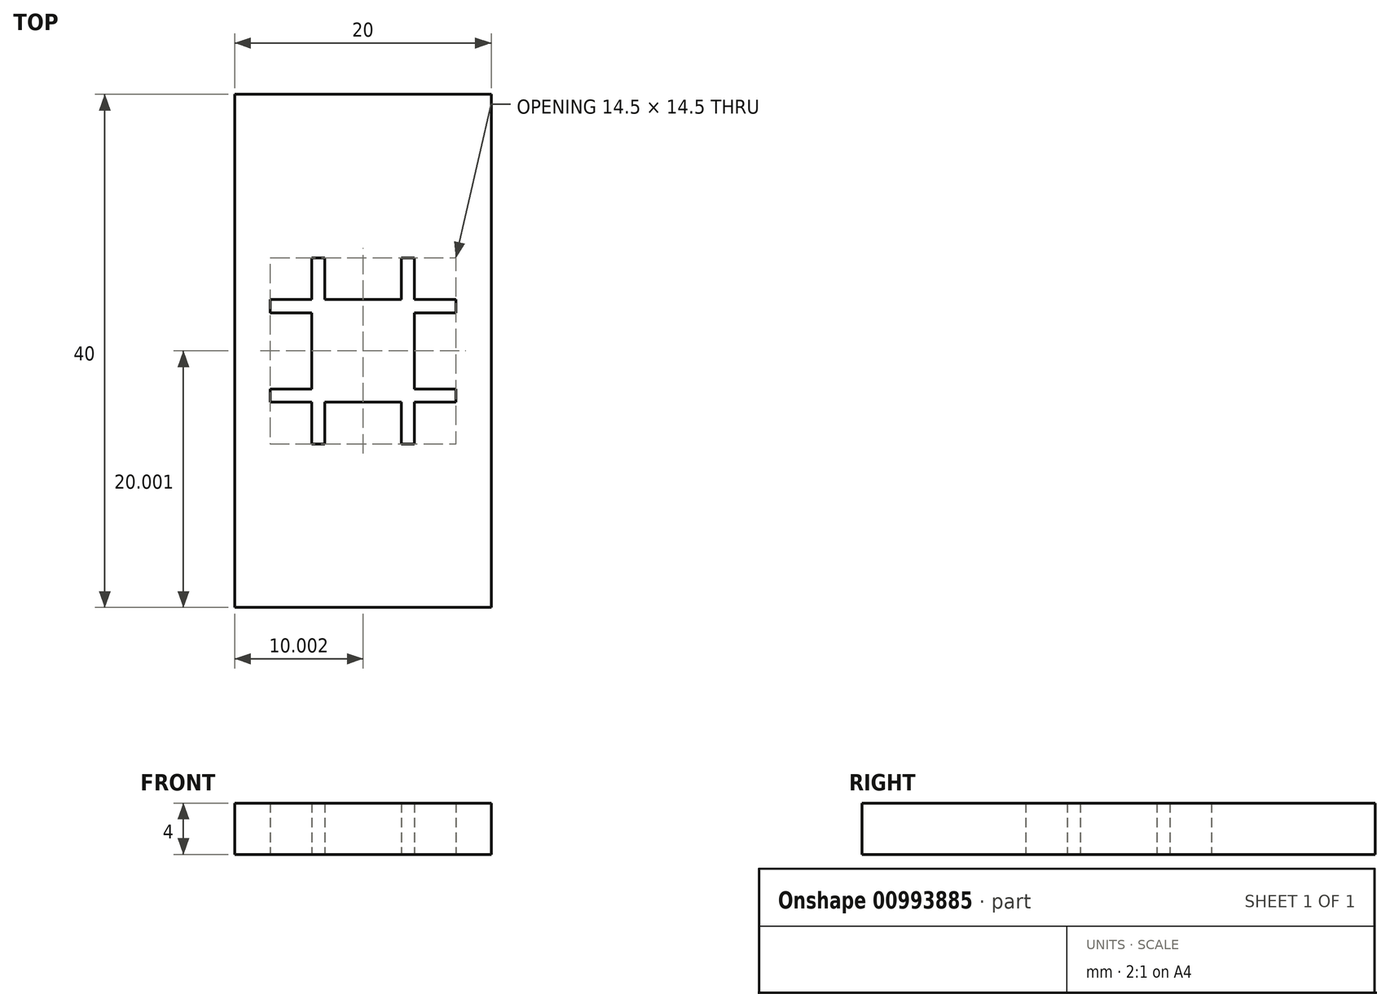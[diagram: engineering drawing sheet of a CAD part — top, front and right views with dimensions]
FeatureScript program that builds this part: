
annotation { "Feature Type Name" : "Feature", "Feature Type Description" : "" }
export const myFeature = defineFeature(function(context is Context, id is Id, definition is map)
    precondition{}
    {
        {
            var Q0;
            Q0=qCreatedBy(makeId("Top.planeOp"),FACE);
            var sketch = newSketch(context, id + "F0", { "sketchPlane" : qUnion([Q0])});
            skLineSegment(sketch, "E0", {"start": v(-4.23, 9.21) * mm, "end": v(-4.23, 12.46) * mm});
            skLineSegment(sketch, "E1", {"start": v(-4.23, 12.46) * mm, "end": v(-5.25, 12.46) * mm});
            skLineSegment(sketch, "E2", {"start": v(-5.25, 12.46) * mm, "end": v(-5.25, 9.21) * mm});
            skLineSegment(sketch, "E3", {"start": v(-5.25, 9.21) * mm, "end": v(-8.5, 9.21) * mm});
            skLineSegment(sketch, "E4", {"start": v(-8.5, 9.21) * mm, "end": v(-8.5, 8.2) * mm});
            skLineSegment(sketch, "E5", {"start": v(-8.5, 8.2) * mm, "end": v(-5.25, 8.2) * mm});
            skLineSegment(sketch, "E6", {"start": v(-5.25, 8.2) * mm, "end": v(-5.25, 2.23) * mm});
            skLineSegment(sketch, "E7", {"start": v(-5.25, 2.23) * mm, "end": v(-8.5, 2.23) * mm});
            skLineSegment(sketch, "E8", {"start": v(-8.5, 2.23) * mm, "end": v(-8.5, 1.21) * mm});
            skLineSegment(sketch, "E9", {"start": v(-8.5, 1.21) * mm, "end": v(-5.25, 1.21) * mm});
            skLineSegment(sketch, "E10", {"start": v(-5.25, 1.21) * mm, "end": v(-5.25, -2.04) * mm});
            skLineSegment(sketch, "E11", {"start": v(-5.25, -2.04) * mm, "end": v(-4.23, -2.04) * mm});
            skLineSegment(sketch, "E12", {"start": v(-4.23, -2.04) * mm, "end": v(-4.23, 1.21) * mm});
            skLineSegment(sketch, "E13", {"start": v(-4.23, 1.21) * mm, "end": v(1.73, 1.21) * mm});
            skLineSegment(sketch, "E14", {"start": v(1.73, 1.21) * mm, "end": v(1.73, -2.04) * mm});
            skLineSegment(sketch, "E15", {"start": v(1.73, -2.04) * mm, "end": v(2.75, -2.04) * mm});
            skLineSegment(sketch, "E16", {"start": v(2.75, -2.04) * mm, "end": v(2.75, 1.21) * mm});
            skLineSegment(sketch, "E17", {"start": v(2.75, 1.21) * mm, "end": v(6, 1.21) * mm});
            skLineSegment(sketch, "E18", {"start": v(6, 1.21) * mm, "end": v(6, 2.23) * mm});
            skLineSegment(sketch, "E19", {"start": v(6, 2.23) * mm, "end": v(2.75, 2.23) * mm});
            skLineSegment(sketch, "E20", {"start": v(2.75, 2.23) * mm, "end": v(2.75, 8.2) * mm});
            skLineSegment(sketch, "E21", {"start": v(2.75, 8.2) * mm, "end": v(6, 8.2) * mm});
            skLineSegment(sketch, "E22", {"start": v(6, 8.2) * mm, "end": v(6, 9.21) * mm});
            skLineSegment(sketch, "E23", {"start": v(6, 9.21) * mm, "end": v(2.75, 9.21) * mm});
            skLineSegment(sketch, "E24", {"start": v(2.75, 9.21) * mm, "end": v(2.75, 12.46) * mm});
            skLineSegment(sketch, "E25", {"start": v(2.75, 12.46) * mm, "end": v(1.73, 12.46) * mm});
            skLineSegment(sketch, "E26", {"start": v(1.73, 12.46) * mm, "end": v(1.73, 9.21) * mm});
            skLineSegment(sketch, "E27", {"start": v(1.73, 9.21) * mm, "end": v(-4.23, 9.21) * mm});
            skLineSegment(sketch, "E28", {"start": v(-1.25, 9.21) * mm, "end": v(-1.25, 1.21) * mm, "construction": true});
            skLineSegment(sketch, "E29", {"start": v(-5.25, 5.21) * mm, "end": v(2.75, 5.21) * mm, "construction": true});
            skLineSegment(sketch, "E30.bottom", {"start": v(8.75, -14.79) * mm, "end": v(-11.25, -14.79) * mm});
            skLineSegment(sketch, "E30.top", {"start": v(8.75, 25.21) * mm, "end": v(-11.25, 25.21) * mm});
            skLineSegment(sketch, "E30.left", {"start": v(8.75, -14.79) * mm, "end": v(8.75, 25.21) * mm});
            skLineSegment(sketch, "E30.right", {"start": v(-11.25, -14.79) * mm, "end": v(-11.25, 25.21) * mm});
            skPoint(sketch, "E30.middle", {"position": v(-1.25, 5.21) * mm});
            skSolve(sketch);
        }
        {
            var Q0;
            Q0=makeQuery(id+"F0.imprint","IMPRINT",FACE,{"disambiguationData":[TD([[makeQuery(id+"F0.imprint","IMPRINT",EDGE,{"derivedFrom":sQuery(id+"F0.wireOp",EDGE,"E0")}),-1.0]])]});
            extrude(context, id + "F1", {"entities" : qUnion([Q0]), "depth" : 4 * mm, "offsetDistance" : 25 * mm});
        }
    });
